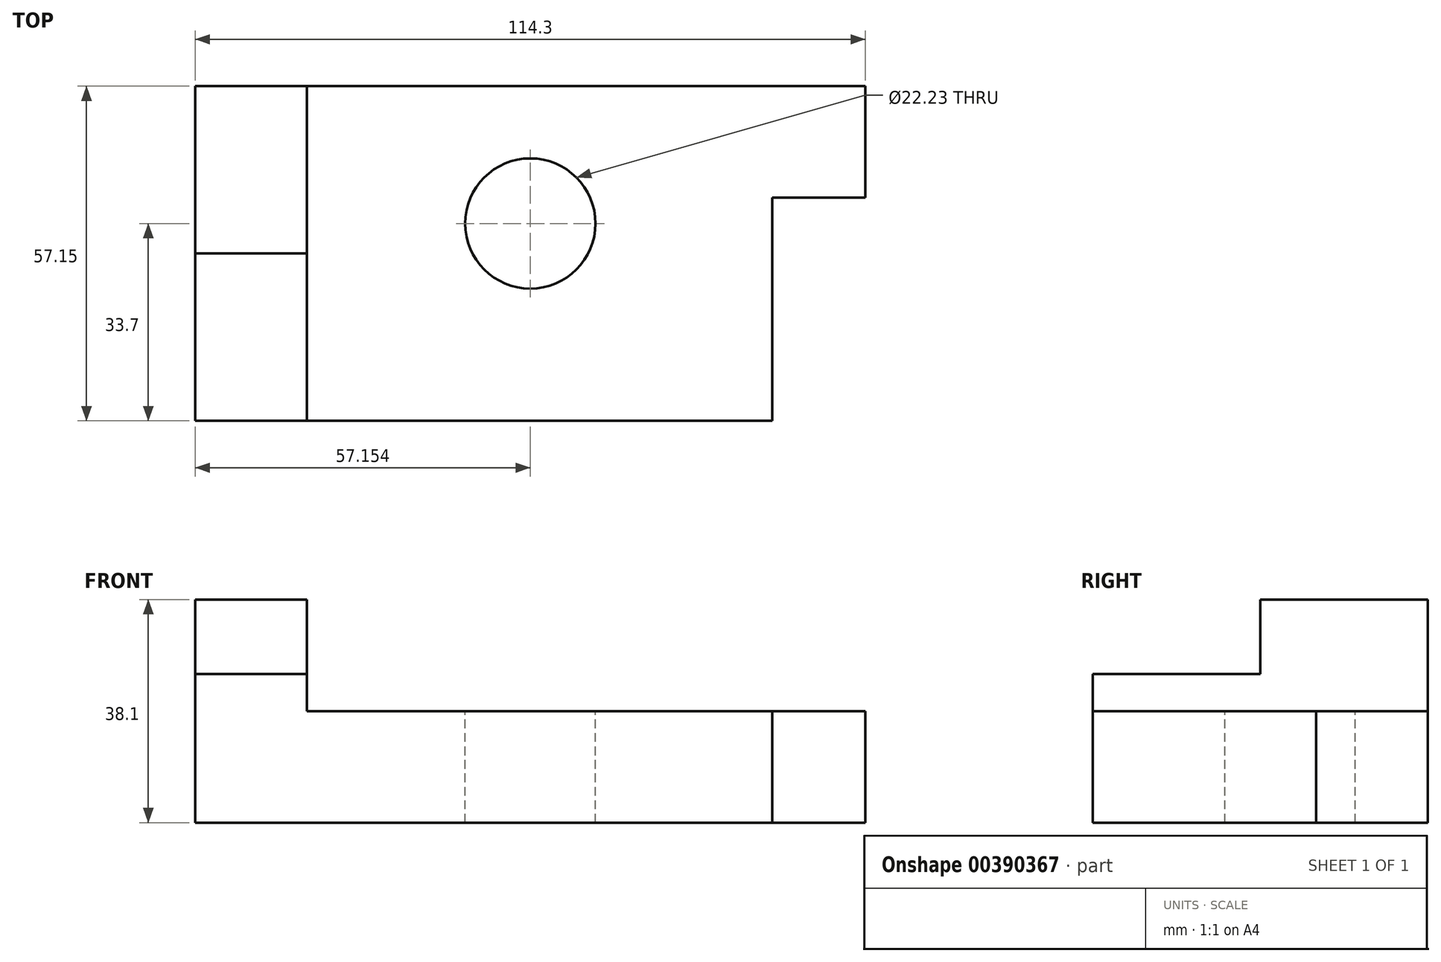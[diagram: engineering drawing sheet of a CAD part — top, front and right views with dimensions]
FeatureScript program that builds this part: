
annotation { "Feature Type Name" : "Feature", "Feature Type Description" : "" }
export const myFeature = defineFeature(function(context is Context, id is Id, definition is map)
    precondition{}
    {
        {
            var Q0;
            Q0=qCreatedBy(makeId("Top.planeOp"),FACE);
            var sketch = newSketch(context, id + "F0", { "sketchPlane" : qUnion([Q0])});
            skLineSegment(sketch, "E0", {"start": v(-33.9, -33.7) * mm, "end": v(80.4, -33.7) * mm});
            skLineSegment(sketch, "E1", {"start": v(80.4, -33.7) * mm, "end": v(80.4, 23.45) * mm});
            skLineSegment(sketch, "E2", {"start": v(80.4, 23.45) * mm, "end": v(-33.9, 23.45) * mm});
            skLineSegment(sketch, "E3", {"start": v(-33.9, 23.45) * mm, "end": v(-33.9, -33.7) * mm});
            skSolve(sketch);
        }
        {
            var Q0;
            Q0=makeQuery(id+"F0.imprint","IMPRINT",FACE,{"disambiguationData":[TD([[makeQuery(id+"F0.imprint","IMPRINT",EDGE,{"derivedFrom":sQuery(id+"F0.wireOp",EDGE,"E0")}),1.0]])]});
            extrude(context, id + "F1", {"entities" : qUnion([Q0]), "depth" : 19.05 * mm});
        }
        {
            var Q0;
            Q0=makeQuery(id+"F1.opExtrude","CAP_FACE",FACE,{"disambiguationData":[OSD([sQuery(id+"F0.wireOp",EDGE,"E0"),sQuery(id+"F0.wireOp",EDGE,"E1"),sQuery(id+"F0.wireOp",EDGE,"E2"),sQuery(id+"F0.wireOp",EDGE,"E3")])],"isStart":false});
            var sketch = newSketch(context, id + "F2", { "sketchPlane" : qUnion([Q0])});
            skLineSegment(sketch, "E4", {"start": v(80.4, -33.7) * mm, "end": v(64.53, -33.7) * mm});
            skLineSegment(sketch, "E5", {"start": v(64.53, -33.7) * mm, "end": v(64.53, 4.4) * mm});
            skLineSegment(sketch, "E6", {"start": v(64.53, 4.4) * mm, "end": v(80.4, 4.4) * mm});
            skSolve(sketch);
        }
        {
            var Q0;
            {var subQ0=sQuery(id+"F2.wireOp",EDGE,"E4");Q0=makeQuery(id+"F2.imprint","IMPRINT",FACE,{"disambiguationData":[TD([[makeQuery(id+"F2.imprint","IMPRINT",EDGE,{"derivedFrom":subQ0}),1.0]])]});}
            extrude(context, id + "F3", {"entities" : qUnion([Q0]), "operationType" : NewBodyOperationType.REMOVE, "oppositeDirection" : true, "depth" : 19.05 * mm});
        }
        {
            var Q0;
            Q0=makeQuery(id+"F1.opExtrude","CAP_FACE",FACE,{"disambiguationData":[OSD([sQuery(id+"F0.wireOp",EDGE,"E0"),sQuery(id+"F0.wireOp",EDGE,"E1"),sQuery(id+"F0.wireOp",EDGE,"E2"),sQuery(id+"F0.wireOp",EDGE,"E3")])],"isStart":false});
            var sketch = newSketch(context, id + "F4", { "sketchPlane" : qUnion([Q0])});
            skLineSegment(sketch, "E7", {"start": v(-33.9, 23.45) * mm, "end": v(-14.85, 23.45) * mm});
            skLineSegment(sketch, "E8", {"start": v(-14.85, 23.45) * mm, "end": v(-14.85, -33.7) * mm});
            skLineSegment(sketch, "E9", {"start": v(-14.85, -33.7) * mm, "end": v(-33.9, -33.7) * mm});
            skLineSegment(sketch, "E10", {"start": v(-33.9, -33.7) * mm, "end": v(-33.9, 23.45) * mm});
            skSolve(sketch);
        }
        {
            var Q0;
            Q0=makeQuery(id+"F4.imprint","IMPRINT",FACE,{"disambiguationData":[TD([[makeQuery(id+"F4.imprint","IMPRINT",EDGE,{"derivedFrom":sQuery(id+"F4.wireOp",EDGE,"E7")}),1.0]])]});
            extrude(context, id + "F5", {"entities" : qUnion([Q0]), "operationType" : NewBodyOperationType.ADD, "depth" : 19.05 * mm});
        }
        {
            var Q0;
            Q0=makeQuery(id+"F5.opExtrude","CAP_FACE",FACE,{"disambiguationData":[OSD([sQuery(id+"F4.wireOp",EDGE,"E7"),sQuery(id+"F4.wireOp",EDGE,"E8"),sQuery(id+"F4.wireOp",EDGE,"E9"),sQuery(id+"F4.wireOp",EDGE,"E10")])],"isStart":false});
            var sketch = newSketch(context, id + "F6", { "sketchPlane" : qUnion([Q0])});
            skLineSegment(sketch, "E11", {"start": v(-33.9, -33.7) * mm, "end": v(-14.85, -33.7) * mm});
            skLineSegment(sketch, "E12", {"start": v(-14.85, -33.7) * mm, "end": v(-14.85, -5.12) * mm});
            skLineSegment(sketch, "E13", {"start": v(-14.85, -5.12) * mm, "end": v(-33.9, -5.12) * mm});
            skLineSegment(sketch, "E14", {"start": v(-33.9, -5.12) * mm, "end": v(-33.9, -33.7) * mm});
            skSolve(sketch);
        }
        {
            var Q0;
            Q0=makeQuery(id+"F6.imprint","IMPRINT",FACE,{"disambiguationData":[TD([[makeQuery(id+"F6.imprint","IMPRINT",EDGE,{"derivedFrom":sQuery(id+"F6.wireOp",EDGE,"E11")}),1.0]])]});
            extrude(context, id + "F7", {"entities" : qUnion([Q0]), "operationType" : NewBodyOperationType.REMOVE, "oppositeDirection" : true, "depth" : 12.7 * mm});
        }
        {
            var Q0;
            Q0=makeQuery(id+"F1.opExtrude","CAP_FACE",FACE,{"disambiguationData":[OSD([sQuery(id+"F0.wireOp",EDGE,"E0"),sQuery(id+"F0.wireOp",EDGE,"E1"),sQuery(id+"F0.wireOp",EDGE,"E2"),sQuery(id+"F0.wireOp",EDGE,"E3")])],"isStart":false});
            var sketch = newSketch(context, id + "F8", { "sketchPlane" : qUnion([Q0])});
            skCircle(sketch, "E15", {"center": v(23.25, 0) * mm, "radius": 11.11 * mm});
            skSolve(sketch);
        }
        {
            var Q0;
            Q0=makeQuery(id+"F8.imprint","IMPRINT",FACE,{"disambiguationData":[TD([[makeQuery(id+"F8.imprint","IMPRINT",EDGE,{"derivedFrom":sQuery(id+"F8.wireOp",EDGE,"E15")}),1.0]])]});
            extrude(context, id + "F9", {"entities" : qUnion([Q0]), "operationType" : NewBodyOperationType.REMOVE, "oppositeDirection" : true, "depth" : 25.4 * mm});
        }
    });
